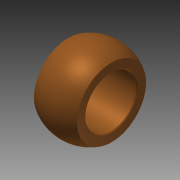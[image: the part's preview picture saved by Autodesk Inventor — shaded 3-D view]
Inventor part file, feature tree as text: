
AUTODESK INVENTOR PART (.ipt)
format: ipt  version: 2014 (Build 180170000, 170)  size: 123,392 bytes
history: native  units: in
note: dims shown in document units (in); Inventor stores cm internally (conversion verified against a paired STEP export)
features: sketch x2, revolve x1, hole x1, chamfer x1
ambient origin geometry x8: Origin, YZ Plane, XZ Plane, XY Plane, X Axis, Y Axis, Z Axis, Center Point
bodies: Solid1 (feature_tree)
feature tree (5):
  revolve  "Revolution1"  [1 undecoded]
  hole  "Hole1"  [1 undecoded]
  chamfer  "Chamfer1"  Distance=0.01in Angle=45.0deg
  sketch  "Sketch1"  dims[d44=0.852in d45=0.5in]
  sketch  "Sketch2"  dims[d46=0.5in d47=90.0deg d48=0.627in d49=0.75in d50=0.375in d51=0.25in d52=0.5635in d53=1.0in d54=0.8108in d55=0.01in d56=0.125in d57=45.0deg]
note: 2 required parameter values undecoded (feature->parameter linkage not recoverable at this tier; creation-order binding heuristic only, values carry confidence <= 0.55)